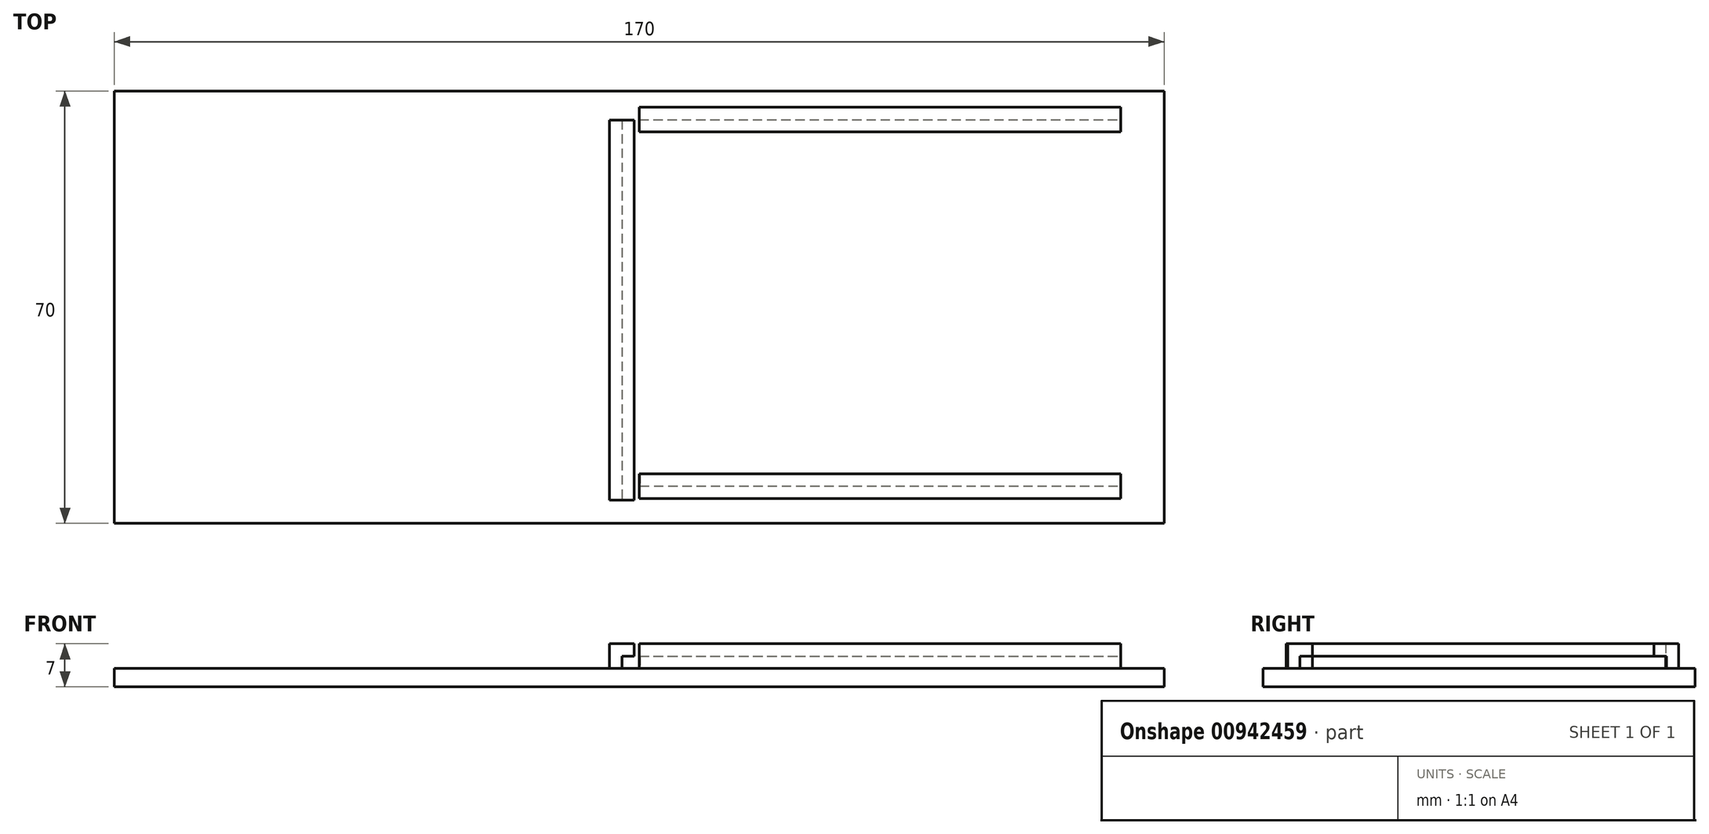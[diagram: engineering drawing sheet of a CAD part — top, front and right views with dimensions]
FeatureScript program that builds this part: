
annotation { "Feature Type Name" : "Feature", "Feature Type Description" : "" }
export const myFeature = defineFeature(function(context is Context, id is Id, definition is map)
    precondition{}
    {
        {
            var Q0;
            Q0=qCreatedBy(makeId("Top.planeOp"),FACE);
            var sketch = newSketch(context, id + "F0", { "sketchPlane" : qUnion([Q0])});
            skLineSegment(sketch, "E0.bottom", {"start": v(-85, 35) * mm, "end": v(85, 35) * mm});
            skLineSegment(sketch, "E0.top", {"start": v(-7, -35) * mm, "end": v(85, -35) * mm});
            skLineSegment(sketch, "E0.left", {"start": v(-85, 35) * mm, "end": v(-85, -25.7) * mm});
            skLineSegment(sketch, "E0.right", {"start": v(85, 35) * mm, "end": v(85, -35) * mm});
            skPoint(sketch, "E0.middle", {"position": v(0, 0) * mm});
            skLineSegment(sketch, "E1.bottom", {"start": v(-85, 14.34) * mm, "end": v(4.03, 14.34) * mm, "construction": true});
            skLineSegment(sketch, "E1.top", {"start": v(-85, -9.97) * mm, "end": v(4.03, -9.97) * mm, "construction": true});
            skLineSegment(sketch, "E1.left", {"start": v(-85, 14.34) * mm, "end": v(-85, -9.97) * mm, "construction": true});
            skLineSegment(sketch, "E2", {"start": v(80.84, 31.5) * mm, "end": v(80.84, 33.5) * mm});
            skLineSegment(sketch, "E3", {"start": v(80.84, 33.5) * mm, "end": v(80.84, 31.5) * mm});
            skLineSegment(sketch, "E4", {"start": v(80.84, -34) * mm, "end": v(80.84, -32) * mm});
            skPoint(sketch, "E5.orphan", {"position": v(82.84, 33.5) * mm});
            skLineSegment(sketch, "E6.bottom", {"start": v(0, 32.35) * mm, "end": v(78, 32.35) * mm});
            skLineSegment(sketch, "E6.top", {"start": v(0, 28.35) * mm, "end": v(78, 28.35) * mm});
            skLineSegment(sketch, "E6.left", {"start": v(0, 32.35) * mm, "end": v(0, 28.35) * mm});
            skLineSegment(sketch, "E6.right", {"start": v(78, 32.35) * mm, "end": v(78, 28.35) * mm});
            skLineSegment(sketch, "E7.bottom", {"start": v(0, -27) * mm, "end": v(78, -27) * mm});
            skLineSegment(sketch, "E7.top", {"start": v(0, -31) * mm, "end": v(78, -31) * mm});
            skLineSegment(sketch, "E7.left", {"start": v(0, -27) * mm, "end": v(0, -31) * mm});
            skLineSegment(sketch, "E7.right", {"start": v(78, -27) * mm, "end": v(78, -31) * mm});
            skLineSegment(sketch, "E8.bottom", {"start": v(-4.8, 30.27) * mm, "end": v(-0.8, 30.27) * mm});
            skLineSegment(sketch, "E8.top", {"start": v(-4.8, -31.23) * mm, "end": v(-0.8, -31.23) * mm});
            skLineSegment(sketch, "E8.left", {"start": v(-4.8, 30.27) * mm, "end": v(-4.8, -31.23) * mm});
            skLineSegment(sketch, "E8.right", {"start": v(-0.8, 30.27) * mm, "end": v(-0.8, -31.23) * mm});
            skLineSegment(sketch, "E9", {"start": v(36.65, 30.5) * mm, "end": v(36.65, -29) * mm, "construction": true});
            skLineSegment(sketch, "E10", {"start": v(-2.8, -31) * mm, "end": v(-2.8, 30.27) * mm, "construction": true});
            skPoint(sketch, "E10.startSnap0", {"position": v(-2.8, -31.23) * mm});
            skLineSegment(sketch, "E11", {"start": v(-2.8, 10.82) * mm, "end": v(77.54, 10.82) * mm, "construction": true});
            skLineSegment(sketch, "E12.top", {"start": v(-85, -35) * mm, "end": v(-7, -35) * mm});
            skLineSegment(sketch, "E12.left", {"start": v(-85, -25.7) * mm, "end": v(-85, -35) * mm});
            skPoint(sketch, "E13.orphan", {"position": v(-85, -35) * mm});
            skSolve(sketch);
        }
        {
            var Q0;
            Q0=makeQuery(id+"F0.imprint","IMPRINT",FACE,{"disambiguationData":[TD([[makeQuery(id+"F0.imprint","IMPRINT",EDGE,{"derivedFrom":sQuery(id+"F0.wireOp",EDGE,"Gt5i3JQ0-8nSh-8WZM-aZxS-6y8rqJcW6WZt.bottom")}),-1.0]])]});
            var Q1;
            {var subQ4=sQuery(id+"F0.wireOp",EDGE,"2e6c90aa-d4f9-48ae-8843-d45dee114d12.0");Q1=makeQuery(id+"F0.imprint","IMPRINT",FACE,{"disambiguationData":[TD([[makeQuery(id+"F0.imprint","IMPRINT",EDGE,{"derivedFrom":subQ4}),1.0]])]});}
            var Q2;
            {var subQ0=sQuery(id+"F0.wireOp",EDGE,"77398701-af11-48c4-a747-01156f786e8b.3");Q2=makeQuery(id+"F0.imprint","IMPRINT",FACE,{"disambiguationData":[TD([[makeQuery(id+"F0.imprint","IMPRINT",EDGE,{"derivedFrom":subQ0}),-1.0]])]});}
            var Q3;
            Q3=makeQuery(id+"F0.imprint","IMPRINT",FACE,{"disambiguationData":[TD([[makeQuery(id+"F0.imprint","IMPRINT",EDGE,{"derivedFrom":sQuery(id+"F0.wireOp",EDGE,"E0.bottom")}),-1.0]])]});
            var Q4;
            Q4=makeQuery(id+"F0.imprint","IMPRINT",FACE,{"disambiguationData":[TD([[makeQuery(id+"F0.imprint","IMPRINT",EDGE,{"derivedFrom":sQuery(id+"F0.wireOp",EDGE,"Gt5i3JQ0-8nSh-8WZM-aZxS-6y8rqJcW6WZt.bottom")}),1.0]])]});
            extrude(context, id + "F1", {"entities" : qUnion([Q0, Q1, Q2, Q3, Q4]), "depth" : 3 * mm, "offsetDistance" : 25 * mm});
        }
        {
            var Q0;
            Q0=makeQuery(id+"F0.imprint","IMPRINT",FACE,{"disambiguationData":[TD([[makeQuery(id+"F0.imprint","IMPRINT",EDGE,{"derivedFrom":sQuery(id+"F0.wireOp",EDGE,"E8.bottom")}),-1.0]])]});
            var Q1;
            Q1=makeQuery(id+"F0.imprint","IMPRINT",FACE,{"disambiguationData":[TD([[makeQuery(id+"F0.imprint","IMPRINT",EDGE,{"derivedFrom":sQuery(id+"F0.wireOp",EDGE,"E7.bottom")}),-1.0]])]});
            var Q2;
            Q2=makeQuery(id+"F0.imprint","IMPRINT",FACE,{"disambiguationData":[TD([[makeQuery(id+"F0.imprint","IMPRINT",EDGE,{"derivedFrom":sQuery(id+"F0.wireOp",EDGE,"E6.bottom")}),-1.0]])]});
            extrude(context, id + "F2", {"entities" : qUnion([Q0, Q1, Q2]), "operationType" : NewBodyOperationType.ADD, "depth" : 7 * mm, "offsetDistance" : 25 * mm});
        }
        {
            var Q0;
            Q0=makeQuery(id+"F2.opExtrude","SWEPT_FACE",FACE,{"disambiguationData":[OSD([sQuery(id+"F0.wireOp",EDGE,"E7.right")])]});
            var sketch = newSketch(context, id + "F3", { "sketchPlane" : qUnion([Q0])});
            skLineSegment(sketch, "E14.bottom", {"start": v(-29, 5) * mm, "end": v(-27, 5) * mm});
            skLineSegment(sketch, "E14.top", {"start": v(-29, 3) * mm, "end": v(-27, 3) * mm});
            skLineSegment(sketch, "E14.left", {"start": v(-29, 5) * mm, "end": v(-29, 3) * mm});
            skLineSegment(sketch, "E14.right", {"start": v(-27, 5) * mm, "end": v(-27, 3) * mm});
            skSolve(sketch);
        }
        {
            var Q0;
            Q0 = qSketchRegion(id + "F3", true);
            extrude(context, id + "F4", {"entities" : qUnion([Q0]), "operationType" : NewBodyOperationType.REMOVE, "oppositeDirection" : true, "depth" : 77.9 * mm, "offsetDistance" : 25 * mm});
        }
        {
            var Q0;
            Q0=makeQuery(id+"F2.opExtrude","SWEPT_FACE",FACE,{"disambiguationData":[OSD([sQuery(id+"F0.wireOp",EDGE,"E8.top")])]});
            var sketch = newSketch(context, id + "F5", { "sketchPlane" : qUnion([Q0])});
            skLineSegment(sketch, "E15.bottom", {"start": v(-2.8, 5) * mm, "end": v(-0.8, 5) * mm});
            skLineSegment(sketch, "E15.top", {"start": v(-2.8, 3) * mm, "end": v(-0.8, 3) * mm});
            skLineSegment(sketch, "E15.left", {"start": v(-2.8, 5) * mm, "end": v(-2.8, 3) * mm});
            skLineSegment(sketch, "E15.right", {"start": v(-0.8, 5) * mm, "end": v(-0.8, 3) * mm});
            skSolve(sketch);
        }
        {
            var Q0;
            Q0=makeQuery(id+"F5.imprint","IMPRINT",FACE,{"disambiguationData":[TD([[makeQuery(id+"F5.imprint","IMPRINT",EDGE,{"derivedFrom":sQuery(id+"F5.wireOp",EDGE,"E15.bottom")}),-1.0]])]});
            extrude(context, id + "F6", {"entities" : qUnion([Q0]), "operationType" : NewBodyOperationType.REMOVE, "oppositeDirection" : true, "depth" : 64.1 * mm, "offsetDistance" : 25 * mm});
        }
        {
            var Q0;
            Q0=makeQuery(id+"F2.opExtrude","SWEPT_FACE",FACE,{"disambiguationData":[OSD([sQuery(id+"F0.wireOp",EDGE,"E6.right")])]});
            var sketch = newSketch(context, id + "F7", { "sketchPlane" : qUnion([Q0])});
            skLineSegment(sketch, "E16.bottom", {"start": v(28.35, 5) * mm, "end": v(30.35, 5) * mm});
            skLineSegment(sketch, "E16.top", {"start": v(28.35, 3) * mm, "end": v(30.35, 3) * mm});
            skLineSegment(sketch, "E16.left", {"start": v(28.35, 5) * mm, "end": v(28.35, 3) * mm});
            skLineSegment(sketch, "E16.right", {"start": v(30.35, 5) * mm, "end": v(30.35, 3) * mm});
            skSolve(sketch);
        }
        {
            var Q0;
            Q0=makeQuery(id+"F7.imprint","IMPRINT",FACE,{"disambiguationData":[TD([[makeQuery(id+"F7.imprint","IMPRINT",EDGE,{"derivedFrom":sQuery(id+"F7.wireOp",EDGE,"E16.bottom")}),-1.0]])]});
            extrude(context, id + "F8", {"entities" : qUnion([Q0]), "operationType" : NewBodyOperationType.REMOVE, "oppositeDirection" : true, "depth" : 78 * mm, "offsetDistance" : 25 * mm});
        }
    });
